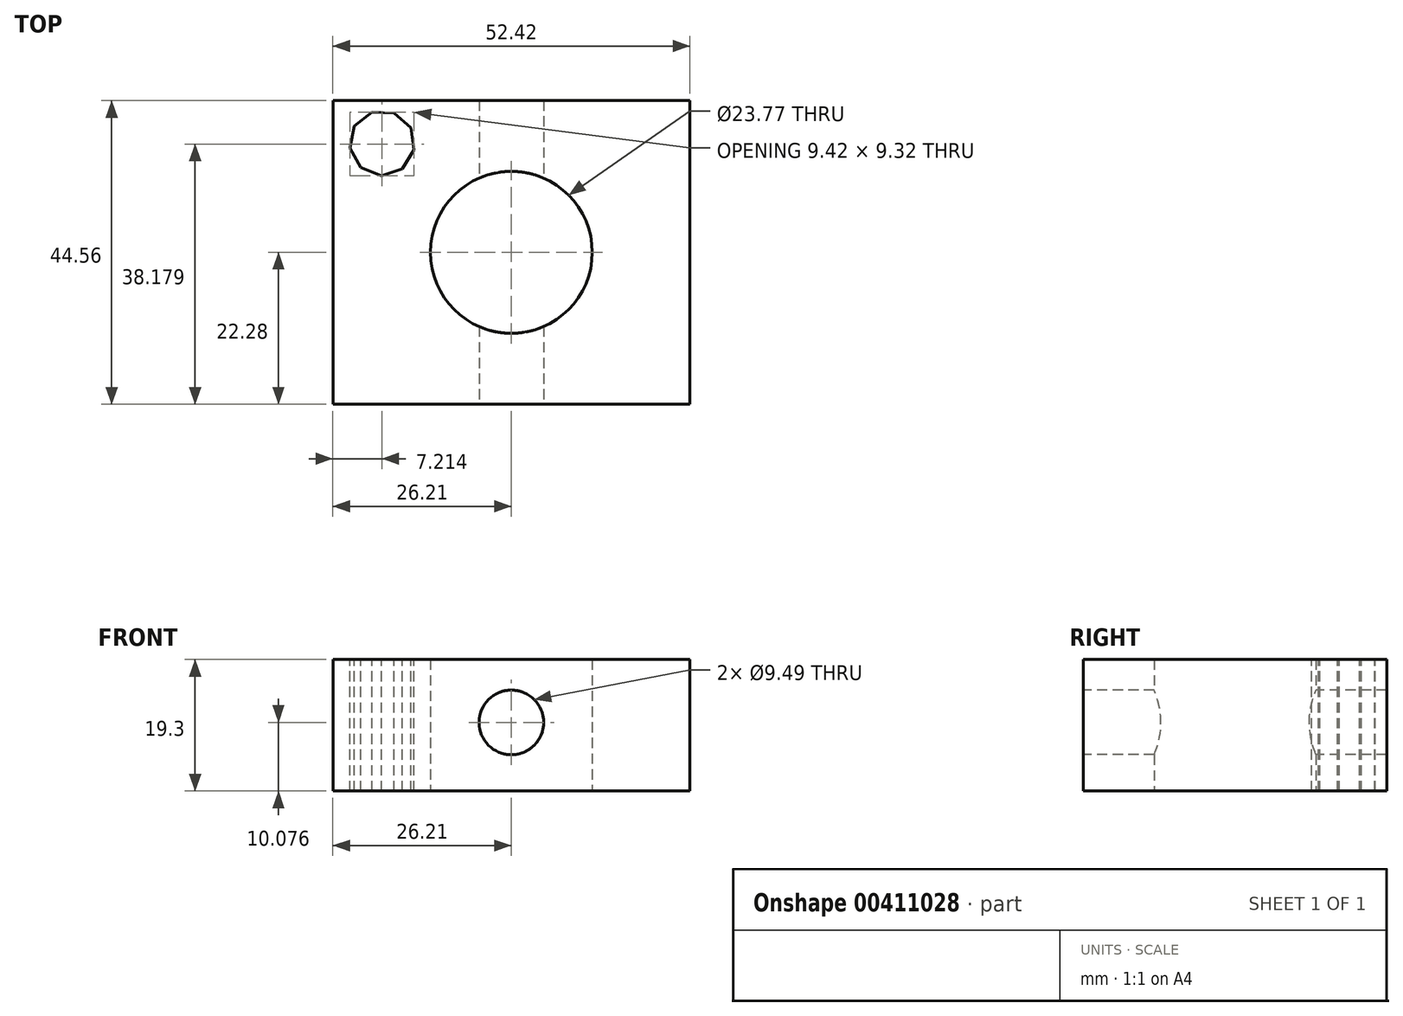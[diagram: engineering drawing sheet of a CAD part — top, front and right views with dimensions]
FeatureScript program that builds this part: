
annotation { "Feature Type Name" : "Feature", "Feature Type Description" : "" }
export const myFeature = defineFeature(function(context is Context, id is Id, definition is map)
    precondition{}
    {
        {
            var Q0;
            Q0=qCreatedBy(makeId("Top.planeOp"),FACE);
            var sketch = newSketch(context, id + "F0", { "sketchPlane" : qUnion([Q0])});
            skLineSegment(sketch, "E0.bottom", {"start": v(-26.2, -22.28) * mm, "end": v(26.2, -22.28) * mm});
            skLineSegment(sketch, "E0.top", {"start": v(-26.2, 22.28) * mm, "end": v(26.2, 22.28) * mm});
            skLineSegment(sketch, "E0.left", {"start": v(-26.2, -22.28) * mm, "end": v(-26.2, 22.28) * mm});
            skLineSegment(sketch, "E0.right", {"start": v(26.2, -22.28) * mm, "end": v(26.2, 22.28) * mm});
            skPoint(sketch, "E0.middle", {"position": v(0, 0) * mm});
            skCircle(sketch, "E1", {"center": v(0, 0) * mm, "radius": 11.88 * mm});
            skSolve(sketch);
        }
        {
            var Q0;
            Q0=makeQuery(id+"F0.imprint","IMPRINT",FACE,{"disambiguationData":[TD([[makeQuery(id+"F0.imprint","IMPRINT",EDGE,{"derivedFrom":sQuery(id+"F0.wireOp",EDGE,"E0.bottom")}),1.0]])]});
            extrude(context, id + "F1", {"entities" : qUnion([Q0]), "depth" : 19.3 * mm});
        }
        {
            var Q0;
            Q0=makeQuery(id+"F1.opExtrude","SWEPT_FACE",FACE,{"disambiguationData":[OSD([sQuery(id+"F0.wireOp",EDGE,"E0.bottom")])]});
            var sketch = newSketch(context, id + "F2", { "sketchPlane" : qUnion([Q0])});
            skCircle(sketch, "E2", {"center": v(0, 10.08) * mm, "radius": 4.75 * mm});
            skSolve(sketch);
        }
        {
            var Q0;
            Q0 = qSketchRegion(id + "F2", true);
            extrude(context, id + "F3", {"entities" : qUnion([Q0]), "operationType" : NewBodyOperationType.REMOVE, "oppositeDirection" : true, "depth" : 58.47 * mm});
        }
        {
            var Q0;
            Q0=makeQuery(id+"F1.opExtrude","CAP_FACE",FACE,{"disambiguationData":[OSD([sQuery(id+"F0.wireOp",EDGE,"E0.bottom"),sQuery(id+"F0.wireOp",EDGE,"E0.top"),sQuery(id+"F0.wireOp",EDGE,"E0.left"),sQuery(id+"F0.wireOp",EDGE,"E0.right"),sQuery(id+"F0.wireOp",EDGE,"E1")])],"isStart":false});
            var sketch = newSketch(context, id + "F4", { "sketchPlane" : qUnion([Q0])});
            skCircle(sketch, "E3.cCircle", {"center": v(-18.97, 16.02) * mm, "radius": 4.5 * mm, "construction": true});
            skLineSegment(sketch, "E3.0", {"start": v(-14.28, 15.07) * mm, "end": v(-16, 12.28) * mm});
            skLineSegment(sketch, "E3.1", {"start": v(-16, 12.28) * mm, "end": v(-19.1, 11.24) * mm});
            skLineSegment(sketch, "E3.2", {"start": v(-19.1, 11.24) * mm, "end": v(-22.14, 12.44) * mm});
            skLineSegment(sketch, "E3.3", {"start": v(-22.14, 12.44) * mm, "end": v(-23.7, 15.31) * mm});
            skLineSegment(sketch, "E3.4", {"start": v(-23.7, 15.31) * mm, "end": v(-23.06, 18.52) * mm});
            skLineSegment(sketch, "E3.5", {"start": v(-23.06, 18.52) * mm, "end": v(-20.5, 20.56) * mm});
            skLineSegment(sketch, "E3.6", {"start": v(-20.5, 20.56) * mm, "end": v(-17.22, 20.48) * mm});
            skLineSegment(sketch, "E3.7", {"start": v(-17.22, 20.48) * mm, "end": v(-14.77, 18.3) * mm});
            skLineSegment(sketch, "E3.8", {"start": v(-14.77, 18.3) * mm, "end": v(-14.28, 15.07) * mm});
            skPoint(sketch, "E3.0.midPoint", {"position": v(-15.14, 13.67) * mm});
            skSolve(sketch);
        }
        {
            var Q0;
            Q0 = qSketchRegion(id + "F4", true);
            extrude(context, id + "F5", {"entities" : qUnion([Q0]), "operationType" : NewBodyOperationType.REMOVE, "oppositeDirection" : true, "depth" : 25.4 * mm});
        }
    });
